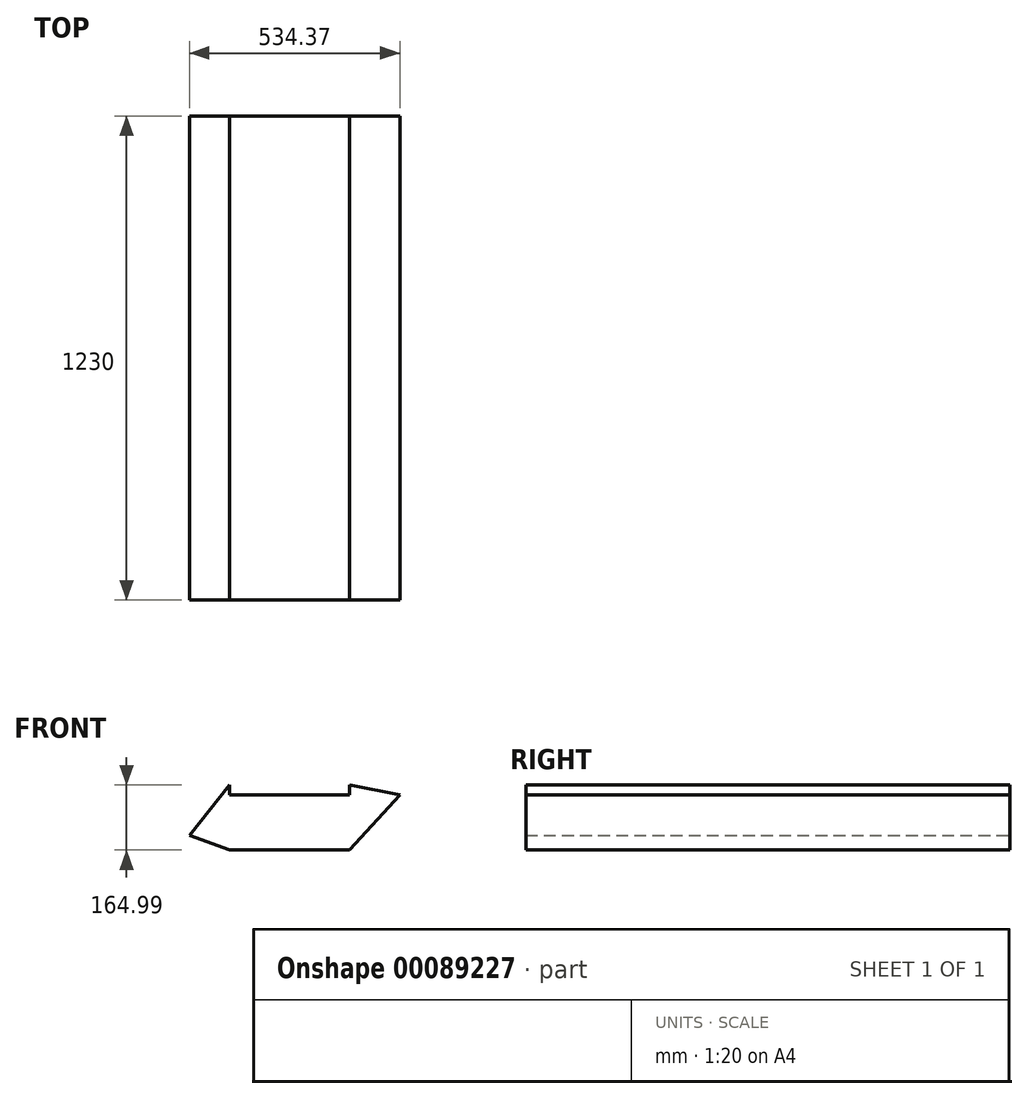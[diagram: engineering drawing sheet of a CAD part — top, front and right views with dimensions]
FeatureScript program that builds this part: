
annotation { "Feature Type Name" : "Feature", "Feature Type Description" : "" }
export const myFeature = defineFeature(function(context is Context, id is Id, definition is map)
    precondition{}
    {
        {
            var Q0;
            Q0=qCreatedBy(makeId("Front.planeOp"),FACE);
            var sketch = newSketch(context, id + "F0", { "sketchPlane" : qUnion([Q0])});
            skLineSegment(sketch, "E0.bottom", {"start": v(-152.31, 79.04) * mm, "end": v(152.31, 79.04) * mm});
            skLineSegment(sketch, "E0.top", {"start": v(-152.31, -85.95) * mm, "end": v(152.31, -85.95) * mm});
            skLineSegment(sketch, "E0.left", {"start": v(-152.31, 79.04) * mm, "end": v(-152.31, -85.95) * mm});
            skLineSegment(sketch, "E0.right", {"start": v(152.31, 79.04) * mm, "end": v(152.31, -85.95) * mm});
            skPoint(sketch, "E0.middle", {"position": v(0, -3.46) * mm});
            skLineSegment(sketch, "E1", {"start": v(-152.31, 79.04) * mm, "end": v(-254.14, -48.33) * mm});
            skLineSegment(sketch, "E2", {"start": v(-254.14, -48.33) * mm, "end": v(-152.31, -85.95) * mm});
            skLineSegment(sketch, "E3", {"start": v(152.31, 79.04) * mm, "end": v(280.23, 53.73) * mm});
            skLineSegment(sketch, "E4", {"start": v(280.23, 53.73) * mm, "end": v(152.31, -85.95) * mm});
            skSolve(sketch);
        }
        {
            var Q0;
            Q0 = qSketchRegion(id + "F0", true);
            extrude(context, id + "F1", {"entities" : qUnion([Q0]), "depth" : 1230 * mm});
        }
        {
            var Q0;
            Q0=makeQuery(id+"F1.opExtrude","SWEPT_FACE",FACE,{"disambiguationData":[OSD([sQuery(id+"F0.wireOp",EDGE,"E0.bottom")])]});
            var sketch = newSketch(context, id + "F2", { "sketchPlane" : qUnion([Q0])});
            skSolve(sketch);
        }
        {
            var Q0;
            {var subQ0=sQuery(id+"F0.wireOp",EDGE,"E0.bottom");Q0=makeQuery(id+"F2.imprint","IMPRINT",FACE,{"disambiguationData":[TD([[makeQuery(id+"F2.imprint","IMPRINT",EDGE,{"derivedFrom":makeQuery(id+"F1.opExtrude","CAP_EDGE",EDGE,{"disambiguationData":[OSD([subQ0])],"isStart":true})}),-1.0]])]});}
            extrude(context, id + "F3", {"entities" : qUnion([Q0]), "operationType" : NewBodyOperationType.REMOVE, "oppositeDirection" : true, "depth" : 25.4 * mm});
        }
    });
